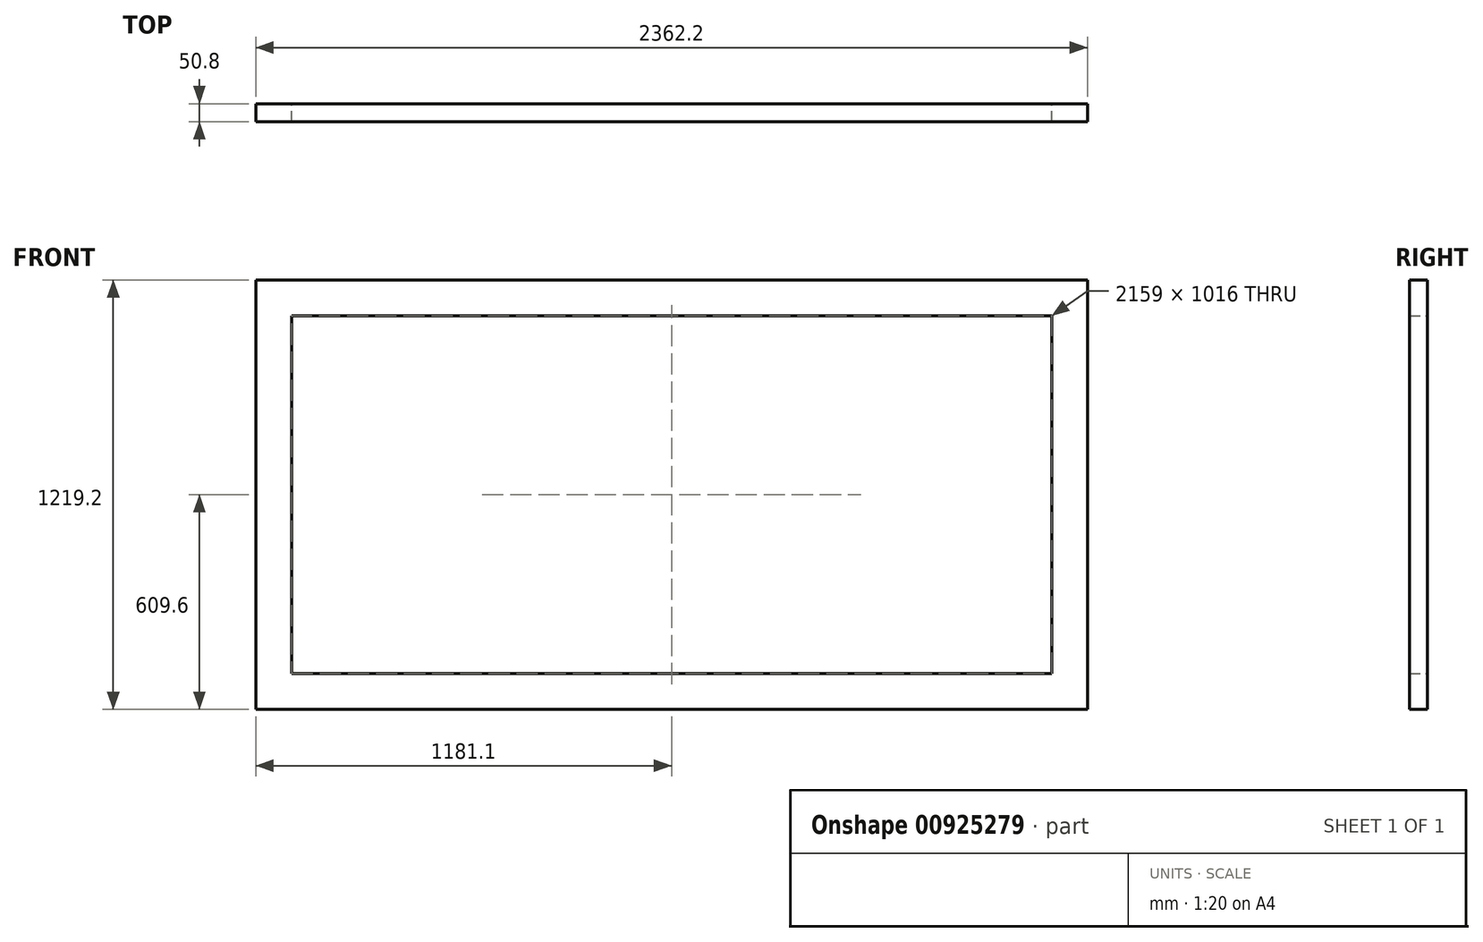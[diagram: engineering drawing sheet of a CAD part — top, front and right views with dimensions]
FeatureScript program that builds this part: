
annotation { "Feature Type Name" : "Feature", "Feature Type Description" : "" }
export const myFeature = defineFeature(function(context is Context, id is Id, definition is map)
    precondition{}
    {
        {
            var Q0;
            Q0=qCreatedBy(makeId("Front.planeOp"),FACE);
            var sketch = newSketch(context, id + "F0", { "sketchPlane" : qUnion([Q0])});
            skLineSegment(sketch, "E0.bottom", {"start": v(0, 0) * mm, "end": v(2362.2, 0) * mm});
            skLineSegment(sketch, "E0.top", {"start": v(0, 1219.2) * mm, "end": v(2362.2, 1219.2) * mm});
            skLineSegment(sketch, "E0.left", {"start": v(0, 0) * mm, "end": v(0, 1219.2) * mm});
            skLineSegment(sketch, "E0.right", {"start": v(2362.2, 0) * mm, "end": v(2362.2, 1219.2) * mm});
            skLineSegment(sketch, "E1.bottom", {"start": v(101.6, 101.6) * mm, "end": v(2260.6, 101.6) * mm});
            skLineSegment(sketch, "E1.top", {"start": v(101.6, 1117.6) * mm, "end": v(2260.6, 1117.6) * mm});
            skLineSegment(sketch, "E1.left", {"start": v(101.6, 101.6) * mm, "end": v(101.6, 1117.6) * mm});
            skLineSegment(sketch, "E1.right", {"start": v(2260.6, 101.6) * mm, "end": v(2260.6, 1117.6) * mm});
            skSolve(sketch);
        }
        {
            var Q0;
            Q0=makeQuery(id+"F0.imprint","IMPRINT",FACE,{"disambiguationData":[TD([[makeQuery(id+"F0.imprint","IMPRINT",EDGE,{"derivedFrom":sQuery(id+"F0.wireOp",EDGE,"E0.bottom")}),1.0]])]});
            extrude(context, id + "F1", {"entities" : qUnion([Q0]), "depth" : 50.8 * mm, "offsetDistance" : 25.4 * mm});
        }
    });
